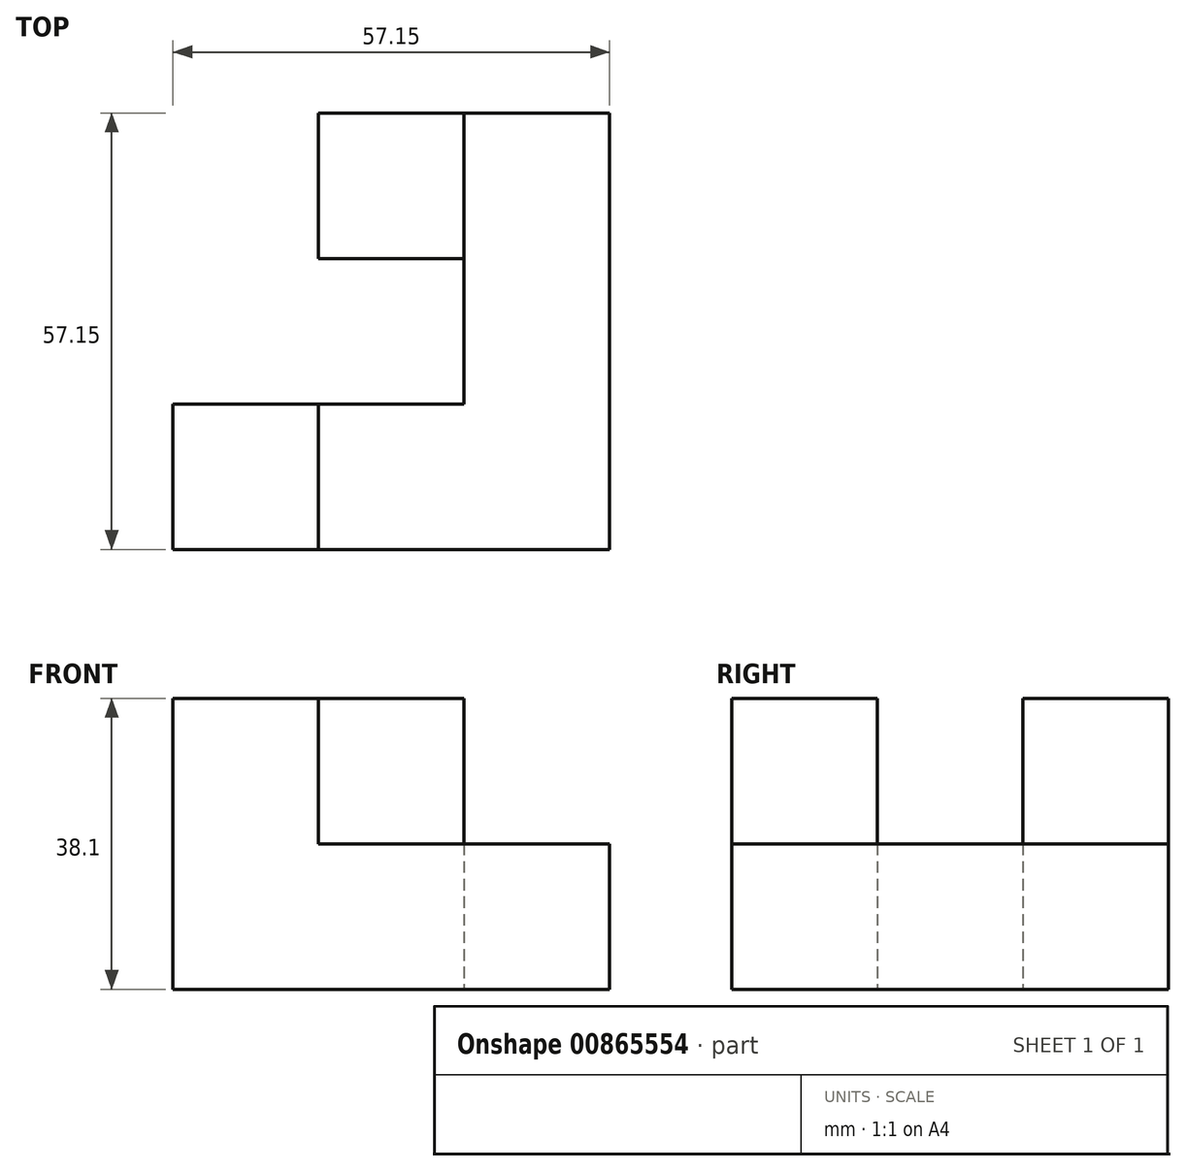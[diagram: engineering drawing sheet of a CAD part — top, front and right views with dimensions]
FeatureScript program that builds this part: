
annotation { "Feature Type Name" : "Feature", "Feature Type Description" : "" }
export const myFeature = defineFeature(function(context is Context, id is Id, definition is map)
    precondition{}
    {
        {
            var Q0;
            Q0=qCreatedBy(makeId("Front.planeOp"),FACE);
            var sketch = newSketch(context, id + "F0", { "sketchPlane" : qUnion([Q0])});
            skLineSegment(sketch, "E0", {"start": v(-25.4, -19.05) * mm, "end": v(31.75, -19.05) * mm});
            skLineSegment(sketch, "E1", {"start": v(31.75, -19.05) * mm, "end": v(31.75, 0) * mm});
            skLineSegment(sketch, "E2", {"start": v(31.75, 0) * mm, "end": v(-6.35, 0) * mm});
            skLineSegment(sketch, "E3", {"start": v(-6.35, 0) * mm, "end": v(-6.35, 19.05) * mm});
            skLineSegment(sketch, "E4", {"start": v(-6.35, 19.05) * mm, "end": v(-25.4, 19.05) * mm});
            skLineSegment(sketch, "E5", {"start": v(-25.4, 19.05) * mm, "end": v(-25.4, -19.05) * mm});
            skSolve(sketch);
        }
        {
            var Q0;
            Q0=makeQuery(id+"F0.imprint","IMPRINT",FACE,{"disambiguationData":[TD([[makeQuery(id+"F0.imprint","IMPRINT",EDGE,{"derivedFrom":sQuery(id+"F0.wireOp",EDGE,"E0")}),1.0]])]});
            extrude(context, id + "F1", {"entities" : qUnion([Q0]), "depth" : 19.05 * mm, "offsetDistance" : 25.4 * mm});
        }
        {
            var Q0;
            Q0=makeQuery(id+"F1.opExtrude","CAP_FACE",FACE,{"disambiguationData":[OSD([sQuery(id+"F0.wireOp",EDGE,"E0"),sQuery(id+"F0.wireOp",EDGE,"E1"),sQuery(id+"F0.wireOp",EDGE,"E2"),sQuery(id+"F0.wireOp",EDGE,"E3"),sQuery(id+"F0.wireOp",EDGE,"E4"),sQuery(id+"F0.wireOp",EDGE,"E5")])],"isStart":true});
            var sketch = newSketch(context, id + "F2", { "sketchPlane" : qUnion([Q0])});
            skLineSegment(sketch, "E6", {"start": v(-12.7, 0) * mm, "end": v(-12.7, -19.05) * mm});
            skPoint(sketch, "E6.endSnap0", {"position": v(-3.18, -19.05) * mm});
            skSolve(sketch);
        }
        {
            var Q0;
            {var subQ0=sQuery(id+"F2.wireOp",EDGE,"E6");Q0=makeQuery(id+"F2.imprint","IMPRINT",FACE,{"disambiguationData":[TD([[makeQuery(id+"F2.imprint","IMPRINT",EDGE,{"derivedFrom":subQ0}),-1.0]])]});}
            extrude(context, id + "F3", {"entities" : qUnion([Q0]), "operationType" : NewBodyOperationType.ADD, "depth" : 38.1 * mm, "offsetDistance" : 25.4 * mm});
        }
        {
            var Q0;
            Q0=makeQuery(id+"F3.opExtrude","SWEPT_FACE",FACE,{"disambiguationData":[OSD([sQuery(id+"F2.wireOp",EDGE,"E6")])]});
            var sketch = newSketch(context, id + "F4", { "sketchPlane" : qUnion([Q0])});
            skLineSegment(sketch, "E7", {"start": v(-19.05, 0) * mm, "end": v(-19.05, -19.05) * mm});
            skSolve(sketch);
        }
        {
            var Q0;
            {var subQ0=sQuery(id+"F4.wireOp",EDGE,"E7");Q0=makeQuery(id+"F4.imprint","IMPRINT",FACE,{"disambiguationData":[TD([[makeQuery(id+"F4.imprint","IMPRINT",EDGE,{"derivedFrom":subQ0}),-1.0]])]});}
            extrude(context, id + "F5", {"entities" : qUnion([Q0]), "operationType" : NewBodyOperationType.ADD, "depth" : 19.05 * mm, "offsetDistance" : 25.4 * mm});
        }
        {
            var Q0;
            {var subQ0=sQuery(id+"F0.wireOp",EDGE,"E2");Q0=makeQuery(id+"F5.boolean.opBoolean","MERGE",FACE,{"derivedFrom":[makeQuery(id+"F3.boolean.opBoolean","MERGE",FACE,{"derivedFrom":[makeQuery(id+"F1.opExtrude","SWEPT_FACE",FACE,{"disambiguationData":[OSD([subQ0])]}),makeQuery(id+"F3.opExtrude","SWEPT_FACE",FACE,{"disambiguationData":[OSD([subQ0])]})]}),makeQuery(id+"F5.opExtrude","SWEPT_FACE",FACE,{"disambiguationData":[OSD([subQ0,sQuery(id+"F2.wireOp",EDGE,"E6")])]})]});}
            var sketch = newSketch(context, id + "F6", { "sketchPlane" : qUnion([Q0])});
            skLineSegment(sketch, "E8", {"start": v(12.7, 19.05) * mm, "end": v(12.7, 38.1) * mm});
            skSolve(sketch);
        }
        {
            var Q0;
            {var subQ0=sQuery(id+"F6.wireOp",EDGE,"E8");Q0=makeQuery(id+"F6.imprint","IMPRINT",FACE,{"disambiguationData":[TD([[makeQuery(id+"F6.imprint","IMPRINT",EDGE,{"derivedFrom":subQ0}),1.0]])]});}
            extrude(context, id + "F7", {"entities" : qUnion([Q0]), "operationType" : NewBodyOperationType.ADD, "depth" : 19.05 * mm, "offsetDistance" : 25.4 * mm});
        }
    });
